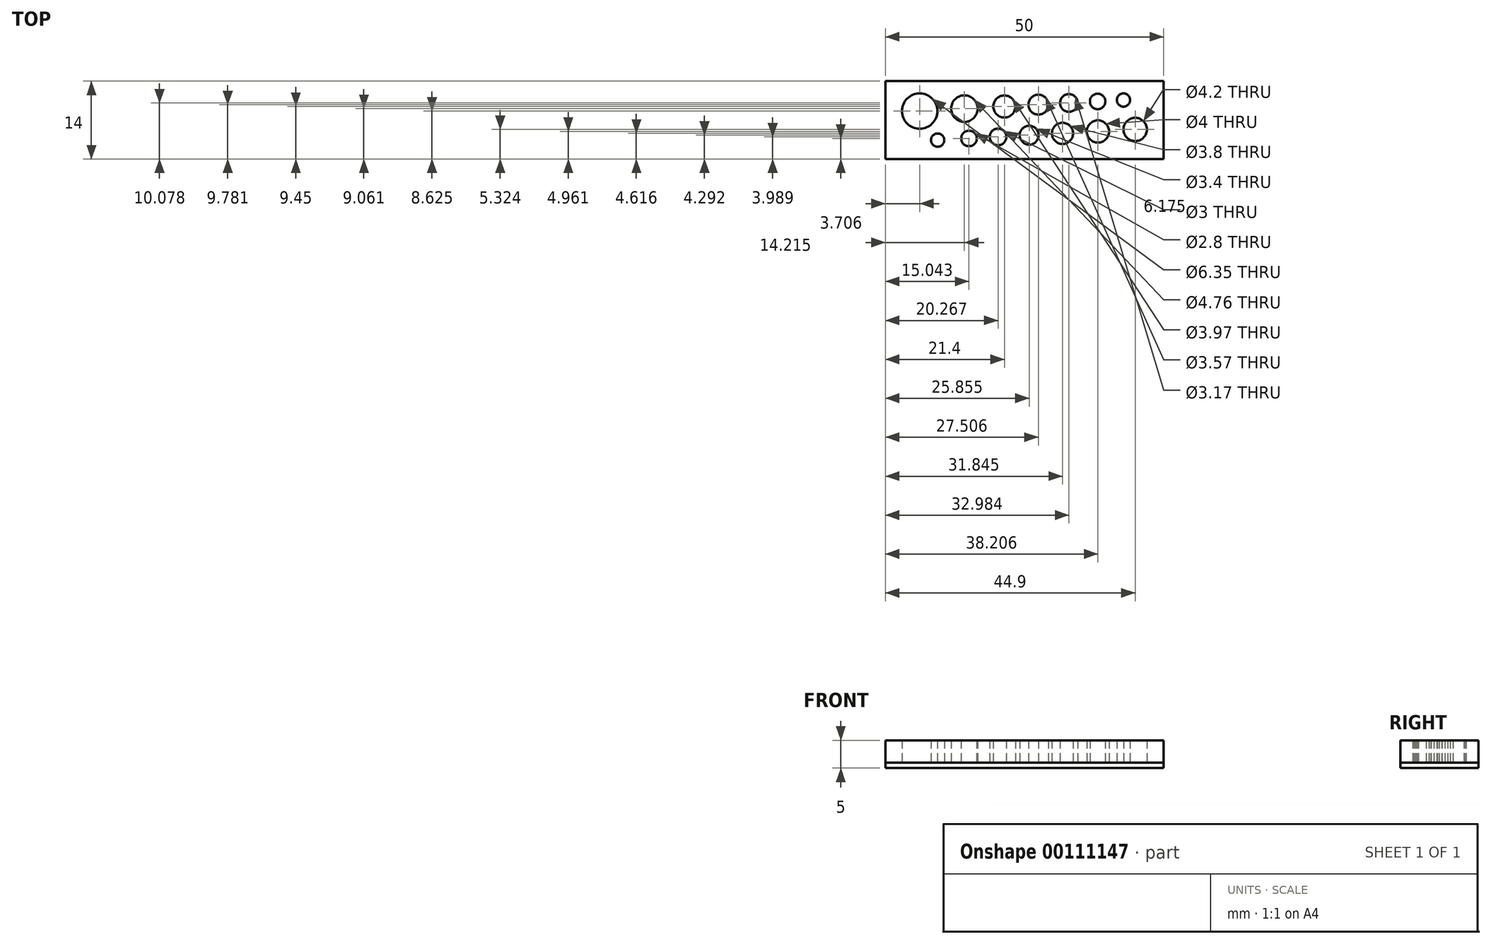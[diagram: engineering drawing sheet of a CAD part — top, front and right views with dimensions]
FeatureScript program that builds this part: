
annotation { "Feature Type Name" : "Feature", "Feature Type Description" : "" }
export const myFeature = defineFeature(function(context is Context, id is Id, definition is map)
    precondition{}
    {
        {
            var Q0;
            Q0=qCreatedBy(makeId("Top.planeOp"),FACE);
            var sketch = newSketch(context, id + "F0", { "sketchPlane" : qUnion([Q0])});
            skLineSegment(sketch, "E0.rect.bottom", {"start": v(25, 7) * mm, "end": v(-25, 7) * mm});
            skLineSegment(sketch, "E0.rect.top", {"start": v(25, -7) * mm, "end": v(-25, -7) * mm});
            skLineSegment(sketch, "E0.rect.left", {"start": v(25, 7) * mm, "end": v(25, -7) * mm});
            skLineSegment(sketch, "E0.rect.right", {"start": v(-25, 7) * mm, "end": v(-25, -7) * mm});
            skPoint(sketch, "E0.rect.middle", {"position": v(0, 0) * mm});
            skLineSegment(sketch, "E1", {"start": v(-25, 1.3) * mm, "end": v(25, 4) * mm, "construction": true});
            skLineSegment(sketch, "E2", {"start": v(-25, -4.1) * mm, "end": v(25, -1.4) * mm, "construction": true});
            skCircle(sketch, "E3", {"center": v(13.15, 3.36) * mm, "radius": 1.39 * mm});
            skCircle(sketch, "E4", {"center": v(7.98, 3.08) * mm, "radius": 1.59 * mm});
            skCircle(sketch, "E5", {"center": v(2.5, 2.78) * mm, "radius": 1.79 * mm});
            skCircle(sketch, "E6", {"center": v(-3.6, 2.45) * mm, "radius": 1.98 * mm});
            skCircle(sketch, "E7", {"center": v(-10.79, 2.06) * mm, "radius": 2.38 * mm});
            skCircle(sketch, "E8", {"center": v(-18.83, 1.62) * mm, "radius": 3.18 * mm});
            skCircle(sketch, "E9", {"center": v(17.8, 3.6) * mm, "radius": 1.2 * mm});
            skCircle(sketch, "E10", {"center": v(-9.96, -3.3) * mm, "radius": 1.4 * mm});
            skCircle(sketch, "E11", {"center": v(-4.73, -3.01) * mm, "radius": 1.5 * mm});
            skCircle(sketch, "E12", {"center": v(0.86, -2.7) * mm, "radius": 1.7 * mm});
            skCircle(sketch, "E13", {"center": v(6.84, -2.38) * mm, "radius": 1.9 * mm});
            skCircle(sketch, "E14", {"center": v(13.2, -2.04) * mm, "radius": 2 * mm});
            skCircle(sketch, "E15", {"center": v(19.9, -1.68) * mm, "radius": 2.1 * mm});
            skLineSegment(sketch, "E16", {"start": v(-23.58, 4.8) * mm, "end": v(23.45, 4.8) * mm, "construction": true});
            skLineSegment(sketch, "E17", {"start": v(23.58, -4.8) * mm, "end": v(-23.27, -4.8) * mm, "construction": true});
            skCircle(sketch, "E18", {"center": v(-15.6, -3.6) * mm, "radius": 1.2 * mm});
            skSolve(sketch);
        }
        {
            var Q0;
            Q0=qSketchRegion(id+"F0",true);
            var Q1;
            Q1=makeQuery(id+"F0.imprint","IMPRINT",FACE,{"disambiguationData":[TD([[makeQuery(id+"F0.imprint","IMPRINT",EDGE,{"derivedFrom":sQuery(id+"F0.wireOp",EDGE,"E8")}),1.0]])]});
            var Q2;
            Q2=makeQuery(id+"F0.imprint","IMPRINT",FACE,{"disambiguationData":[TD([[makeQuery(id+"F0.imprint","IMPRINT",EDGE,{"derivedFrom":sQuery(id+"F0.wireOp",EDGE,"E7")}),1.0]])]});
            var Q3;
            Q3=makeQuery(id+"F0.imprint","IMPRINT",FACE,{"disambiguationData":[TD([[makeQuery(id+"F0.imprint","IMPRINT",EDGE,{"derivedFrom":sQuery(id+"F0.wireOp",EDGE,"E6")}),1.0]])]});
            var Q4;
            Q4=makeQuery(id+"F0.imprint","IMPRINT",FACE,{"disambiguationData":[TD([[makeQuery(id+"F0.imprint","IMPRINT",EDGE,{"derivedFrom":sQuery(id+"F0.wireOp",EDGE,"E5")}),1.0]])]});
            var Q5;
            Q5=makeQuery(id+"F0.imprint","IMPRINT",FACE,{"disambiguationData":[TD([[makeQuery(id+"F0.imprint","IMPRINT",EDGE,{"derivedFrom":sQuery(id+"F0.wireOp",EDGE,"E4")}),1.0]])]});
            var Q6;
            Q6=makeQuery(id+"F0.imprint","IMPRINT",FACE,{"disambiguationData":[TD([[makeQuery(id+"F0.imprint","IMPRINT",EDGE,{"derivedFrom":sQuery(id+"F0.wireOp",EDGE,"E3")}),1.0]])]});
            var Q7;
            Q7=makeQuery(id+"F0.imprint","IMPRINT",FACE,{"disambiguationData":[TD([[makeQuery(id+"F0.imprint","IMPRINT",EDGE,{"derivedFrom":sQuery(id+"F0.wireOp",EDGE,"E9")}),1.0]])]});
            var Q8;
            Q8=makeQuery(id+"F0.imprint","IMPRINT",FACE,{"disambiguationData":[TD([[makeQuery(id+"F0.imprint","IMPRINT",EDGE,{"derivedFrom":sQuery(id+"F0.wireOp",EDGE,"E18")}),1.0]])]});
            var Q9;
            Q9=makeQuery(id+"F0.imprint","IMPRINT",FACE,{"disambiguationData":[TD([[makeQuery(id+"F0.imprint","IMPRINT",EDGE,{"derivedFrom":sQuery(id+"F0.wireOp",EDGE,"E10")}),1.0]])]});
            var Q10;
            Q10=makeQuery(id+"F0.imprint","IMPRINT",FACE,{"disambiguationData":[TD([[makeQuery(id+"F0.imprint","IMPRINT",EDGE,{"derivedFrom":sQuery(id+"F0.wireOp",EDGE,"E11")}),1.0]])]});
            var Q11;
            Q11=makeQuery(id+"F0.imprint","IMPRINT",FACE,{"disambiguationData":[TD([[makeQuery(id+"F0.imprint","IMPRINT",EDGE,{"derivedFrom":sQuery(id+"F0.wireOp",EDGE,"E12")}),1.0]])]});
            var Q12;
            Q12=makeQuery(id+"F0.imprint","IMPRINT",FACE,{"disambiguationData":[TD([[makeQuery(id+"F0.imprint","IMPRINT",EDGE,{"derivedFrom":sQuery(id+"F0.wireOp",EDGE,"E13")}),1.0]])]});
            var Q13;
            Q13=makeQuery(id+"F0.imprint","IMPRINT",FACE,{"disambiguationData":[TD([[makeQuery(id+"F0.imprint","IMPRINT",EDGE,{"derivedFrom":sQuery(id+"F0.wireOp",EDGE,"E14")}),1.0]])]});
            var Q14;
            Q14=makeQuery(id+"F0.imprint","IMPRINT",FACE,{"disambiguationData":[TD([[makeQuery(id+"F0.imprint","IMPRINT",EDGE,{"derivedFrom":sQuery(id+"F0.wireOp",EDGE,"E15")}),1.0]])]});
            extrude(context, id + "F1", {"entities" : qUnion([Q0, Q1, Q2, Q3, Q4, Q5, Q6, Q7, Q8, Q9, Q10, Q11, Q12, Q13, Q14]), "oppositeDirection" : true, "depth" : 1 * mm});
        }
        {
            var Q0;
            Q0=qSketchRegion(id+"F0",true);
            extrude(context, id + "F2", {"entities" : qUnion([Q0]), "depth" : 4 * mm});
        }
    });
